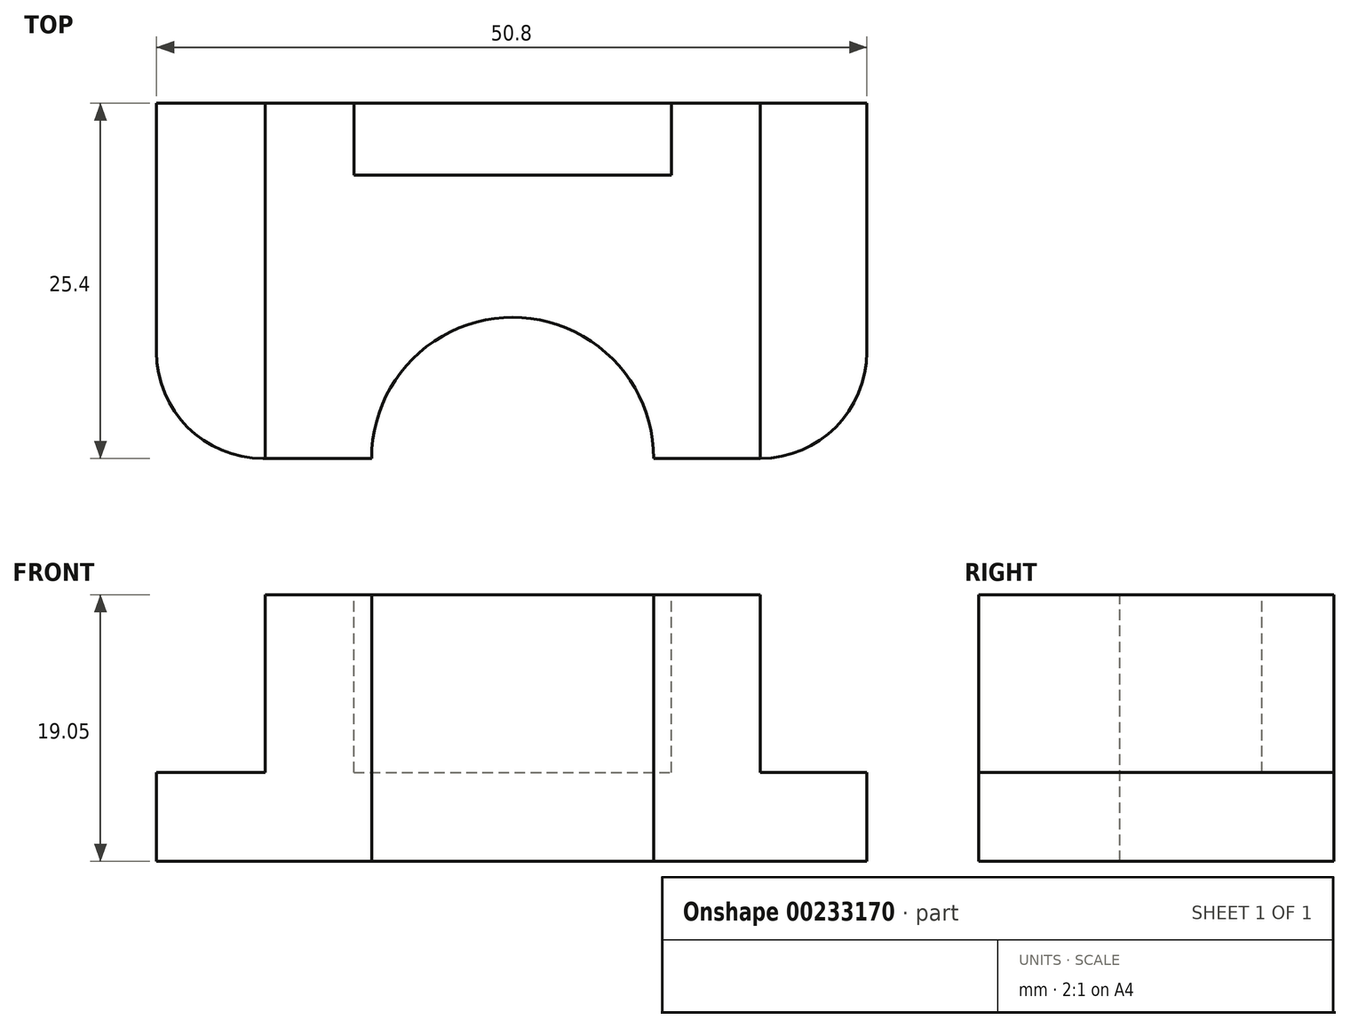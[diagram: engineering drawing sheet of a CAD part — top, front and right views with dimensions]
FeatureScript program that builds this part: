
annotation { "Feature Type Name" : "Feature", "Feature Type Description" : "" }
export const myFeature = defineFeature(function(context is Context, id is Id, definition is map)
    precondition{}
    {
        {
            var Q0;
            Q0=qCreatedBy(makeId("Top.planeOp"),FACE);
            var sketch = newSketch(context, id + "F0", { "sketchPlane" : qUnion([Q0])});
            skLineSegment(sketch, "E0.bottom", {"start": v(-19.72, 2.34) * mm, "end": v(31.08, 2.34) * mm});
            skLineSegment(sketch, "E0.top", {"start": v(-19.72, -23.06) * mm, "end": v(31.08, -23.06) * mm});
            skLineSegment(sketch, "E0.left", {"start": v(-19.72, 2.34) * mm, "end": v(-19.72, -23.06) * mm});
            skLineSegment(sketch, "E0.right", {"start": v(31.08, 2.34) * mm, "end": v(31.08, -23.06) * mm});
            skSolve(sketch);
        }
        {
            var Q0;
            Q0=makeQuery(id+"F0.imprint","IMPRINT",FACE,{"disambiguationData":[TD([[makeQuery(id+"F0.imprint","IMPRINT",EDGE,{"derivedFrom":sQuery(id+"F0.wireOp",EDGE,"E0.bottom")}),-1.0]])]});
            extrude(context, id + "F1", {"entities" : qUnion([Q0]), "depth" : 6.35 * mm});
        }
        {
            var Q0;
            Q0=makeQuery(id+"F1.opExtrude","SWEPT_EDGE",EDGE,{"disambiguationData":[OSD([sQuery(id+"F0.wireOp",EDGE,"E0.top"),sQuery(id+"F0.wireOp",EDGE,"E0.left")])]});
            var Q1;
            Q1=makeQuery(id+"F1.opExtrude","SWEPT_EDGE",EDGE,{"disambiguationData":[OSD([sQuery(id+"F0.wireOp",EDGE,"E0.top"),sQuery(id+"F0.wireOp",EDGE,"E0.right")])]});
            fillet(context, id + "F2", {"entities" : qUnion([Q0, Q1]), "radius" : 7.62 * mm, "tangentPropagation" : true, "allowEdgeOverflow" : false});
        }
        {
            var Q0;
            Q0=makeQuery(id+"F1.opExtrude","CAP_FACE",FACE,{"disambiguationData":[OSD([sQuery(id+"F0.wireOp",EDGE,"E0.bottom"),sQuery(id+"F0.wireOp",EDGE,"E0.top"),sQuery(id+"F0.wireOp",EDGE,"E0.left"),sQuery(id+"F0.wireOp",EDGE,"E0.right")])],"isStart":false});
            var sketch = newSketch(context, id + "F3", { "sketchPlane" : qUnion([Q0])});
            skLineSegment(sketch, "E1.bottom", {"start": v(-11.96, 2.34) * mm, "end": v(23.46, 2.34) * mm});
            skLineSegment(sketch, "E1.top", {"start": v(-11.96, -23.06) * mm, "end": v(23.46, -23.06) * mm});
            skLineSegment(sketch, "E1.left", {"start": v(-11.96, 2.34) * mm, "end": v(-11.96, -23.06) * mm});
            skLineSegment(sketch, "E1.right", {"start": v(23.46, 2.34) * mm, "end": v(23.46, -23.06) * mm});
            skSolve(sketch);
        }
        {
            var Q0;
            Q0=makeQuery(id+"F3.imprint","IMPRINT",FACE,{"disambiguationData":[TD([[makeQuery(id+"F3.imprint","IMPRINT",EDGE,{"derivedFrom":sQuery(id+"F3.wireOp",EDGE,"E1.bottom")}),-1.0]])]});
            extrude(context, id + "F4", {"entities" : qUnion([Q0]), "operationType" : NewBodyOperationType.ADD, "depth" : 12.7 * mm});
        }
        {
            var Q0;
            Q0=makeQuery(id+"F4.opExtrude","CAP_FACE",FACE,{"disambiguationData":[OSD([sQuery(id+"F3.wireOp",EDGE,"E1.bottom"),sQuery(id+"F3.wireOp",EDGE,"E1.top"),sQuery(id+"F3.wireOp",EDGE,"E1.left"),sQuery(id+"F3.wireOp",EDGE,"E1.right")])],"isStart":false});
            var sketch = newSketch(context, id + "F5", { "sketchPlane" : qUnion([Q0])});
            skArc(sketch, "E2", {"start": v(15.84, -23.06) * mm, "mid": v(5.75, -12.97) * mm, "end": v(-4.34, -23.06) * mm});
            skSolve(sketch);
        }
        {
            var Q0;
            {var subQ0=sQuery(id+"F5.wireOp",EDGE,"E2");Q0=makeQuery(id+"F5.imprint","IMPRINT",FACE,{"disambiguationData":[TD([[makeQuery(id+"F5.imprint","IMPRINT",EDGE,{"derivedFrom":subQ0}),1.0]])]});}
            extrude(context, id + "F6", {"entities" : qUnion([Q0]), "operationType" : NewBodyOperationType.REMOVE, "endBound" : BoundingType.THROUGH_ALL, "oppositeDirection" : true, "depth" : 25.4 * mm});
        }
        {
            var Q0;
            Q0=makeQuery(id+"F4.opExtrude","CAP_FACE",FACE,{"disambiguationData":[OSD([sQuery(id+"F3.wireOp",EDGE,"E1.bottom"),sQuery(id+"F3.wireOp",EDGE,"E1.top"),sQuery(id+"F3.wireOp",EDGE,"E1.left"),sQuery(id+"F3.wireOp",EDGE,"E1.right")])],"isStart":false});
            var sketch = newSketch(context, id + "F7", { "sketchPlane" : qUnion([Q0])});
            skLineSegment(sketch, "E3.bottom", {"start": v(-5.61, 2.34) * mm, "end": v(17.1, 2.34) * mm});
            skLineSegment(sketch, "E3.top", {"start": v(-5.61, -2.81) * mm, "end": v(17.1, -2.81) * mm});
            skLineSegment(sketch, "E3.left", {"start": v(-5.61, 2.34) * mm, "end": v(-5.61, -2.81) * mm});
            skLineSegment(sketch, "E3.right", {"start": v(17.1, 2.34) * mm, "end": v(17.1, -2.81) * mm});
            skSolve(sketch);
        }
        {
            var Q0;
            Q0=makeQuery(id+"F7.imprint","IMPRINT",FACE,{"disambiguationData":[TD([[makeQuery(id+"F7.imprint","IMPRINT",EDGE,{"derivedFrom":sQuery(id+"F7.wireOp",EDGE,"E3.bottom")}),-1.0]])]});
            extrude(context, id + "F8", {"entities" : qUnion([Q0]), "operationType" : NewBodyOperationType.REMOVE, "oppositeDirection" : true, "depth" : 12.7 * mm});
        }
    });
